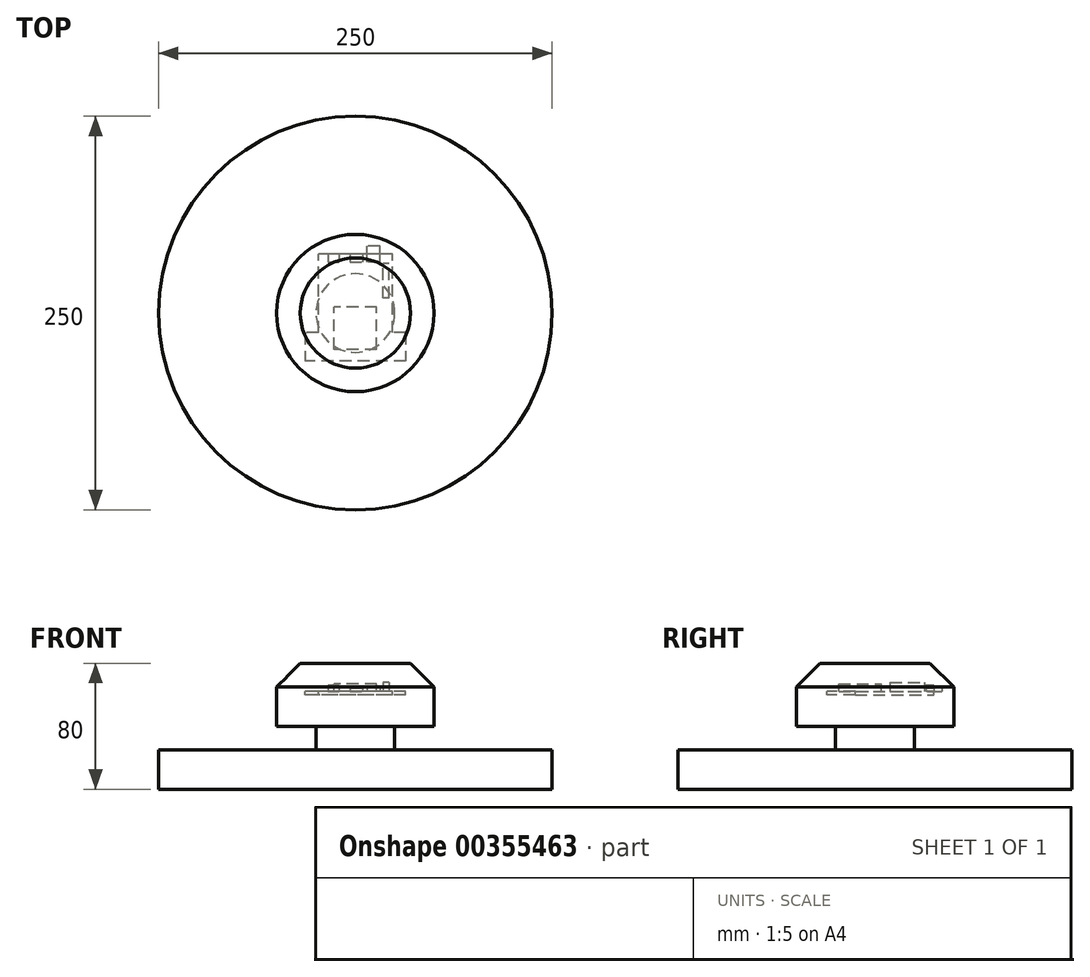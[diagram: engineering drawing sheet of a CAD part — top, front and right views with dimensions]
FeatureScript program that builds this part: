
annotation { "Feature Type Name" : "Feature", "Feature Type Description" : "" }
export const myFeature = defineFeature(function(context is Context, id is Id, definition is map)
    precondition{}
    {
        {
            var Q0;
            Q0=qCreatedBy(makeId("Top.planeOp"),FACE);
            var sketch = newSketch(context, id + "F0", { "sketchPlane" : qUnion([Q0])});
            skLineSegment(sketch, "E0.bottom", {"start": v(13.5, -13.5) * mm, "end": v(-13.5, -13.5) * mm});
            skLineSegment(sketch, "E0.top", {"start": v(13.5, 13.5) * mm, "end": v(-13.5, 13.5) * mm});
            skLineSegment(sketch, "E0.left", {"start": v(13.5, -13.5) * mm, "end": v(13.5, 13.5) * mm});
            skLineSegment(sketch, "E0.right", {"start": v(-13.5, -13.5) * mm, "end": v(-13.5, 13.5) * mm});
            skPoint(sketch, "E0.middle", {"position": v(0, 0) * mm});
            skSolve(sketch);
        }
        {
            var Q0;
            Q0=makeQuery(id+"F0.imprint","IMPRINT",FACE,{"disambiguationData":[TD([[makeQuery(id+"F0.imprint","IMPRINT",EDGE,{"derivedFrom":sQuery(id+"F0.wireOp",EDGE,"E0.bottom")}),-1.0]])]});
            extrude(context, id + "F1", {"entities" : qUnion([Q0]), "oppositeDirection" : true, "depth" : 2 * mm});
        }
        {
            var Q0;
            Q0=makeQuery(id+"F1.opExtrude","CAP_FACE",FACE,{"disambiguationData":[OSD([sQuery(id+"F0.wireOp",EDGE,"E0.bottom"),sQuery(id+"F0.wireOp",EDGE,"E0.top"),sQuery(id+"F0.wireOp",EDGE,"E0.left"),sQuery(id+"F0.wireOp",EDGE,"E0.right")])],"isStart":false});
            cPlane(context, id + "F2", {"entities" : qUnion([Q0]), "cplaneType" : CPlaneType.OFFSET, "offset" : 3 * mm, "width" : 150 * mm, "height" : 150 * mm});
        }
        {
            var Q0;
            Q0=qCreatedBy(id+"F2.planeOp",FACE);
            var sketch = newSketch(context, id + "F3", { "sketchPlane" : qUnion([Q0])});
            skLineSegment(sketch, "E1", {"start": v(0, 0) * mm, "end": v(0, -22) * mm, "construction": true});
            skLineSegment(sketch, "E2.bottom", {"start": v(23.5, 3) * mm, "end": v(-23.5, 3) * mm});
            skLineSegment(sketch, "E2.top", {"start": v(23.5, -47) * mm, "end": v(-23.5, -47) * mm});
            skLineSegment(sketch, "E2.left", {"start": v(23.5, 3) * mm, "end": v(23.5, -47) * mm});
            skLineSegment(sketch, "E2.right", {"start": v(-23.5, 3) * mm, "end": v(-23.5, -47) * mm});
            skPoint(sketch, "E2.middle", {"position": v(0, -22) * mm});
            skSolve(sketch);
        }
        {
            var Q0;
            Q0=makeQuery(id+"F3.imprint","IMPRINT",FACE,{"disambiguationData":[TD([[makeQuery(id+"F3.imprint","IMPRINT",EDGE,{"derivedFrom":sQuery(id+"F3.wireOp",EDGE,"E2.bottom")}),1.0]])]});
            extrude(context, id + "F4", {"entities" : qUnion([Q0]), "depth" : 2 * mm});
        }
        {
            var Q0;
            Q0=makeQuery(id+"F4.opExtrude","CAP_FACE",FACE,{"disambiguationData":[OSD([sQuery(id+"F3.wireOp",EDGE,"E2.bottom"),sQuery(id+"F3.wireOp",EDGE,"E2.top"),sQuery(id+"F3.wireOp",EDGE,"E2.left"),sQuery(id+"F3.wireOp",EDGE,"E2.right")])],"isStart":true});
            var sketch = newSketch(context, id + "F5", { "sketchPlane" : qUnion([Q0])});
            skLineSegment(sketch, "E3", {"start": v(0, -3) * mm, "end": v(0, -12) * mm, "construction": true});
            skPoint(sketch, "E3.endSnap0", {"position": v(0, -3) * mm});
            skLineSegment(sketch, "E4.bottom", {"start": v(32, -3) * mm, "end": v(-32, -3) * mm});
            skLineSegment(sketch, "E4.top", {"start": v(32, -21) * mm, "end": v(-32, -21) * mm});
            skLineSegment(sketch, "E4.left", {"start": v(32, -3) * mm, "end": v(32, -21) * mm});
            skLineSegment(sketch, "E4.right", {"start": v(-32, -3) * mm, "end": v(-32, -21) * mm});
            skPoint(sketch, "E4.middle", {"position": v(0, -12) * mm});
            skSolve(sketch);
        }
        {
            var Q0;
            Q0=makeQuery(id+"F5.imprint","IMPRINT",FACE,{"disambiguationData":[TD([[makeQuery(id+"F5.imprint","IMPRINT",EDGE,{"derivedFrom":sQuery(id+"F5.wireOp",EDGE,"E4.top")}),-1.0]])]});
            extrude(context, id + "F6", {"entities" : qUnion([Q0]), "operationType" : NewBodyOperationType.ADD, "oppositeDirection" : true, "depth" : 2 * mm});
        }
        {
            var Q0;
            Q0=makeQuery(id+"F1.opExtrude","CAP_FACE",FACE,{"disambiguationData":[OSD([sQuery(id+"F0.wireOp",EDGE,"E0.bottom"),sQuery(id+"F0.wireOp",EDGE,"E0.top"),sQuery(id+"F0.wireOp",EDGE,"E0.left"),sQuery(id+"F0.wireOp",EDGE,"E0.right")])],"isStart":false});
            var Q1;
            Q1=makeQuery(id+"F6.boolean.opBoolean","MERGE",FACE,{"derivedFrom":[makeQuery(id+"F4.opExtrude","CAP_FACE",FACE,{"disambiguationData":[OSD([sQuery(id+"F3.wireOp",EDGE,"E2.bottom"),sQuery(id+"F3.wireOp",EDGE,"E2.top"),sQuery(id+"F3.wireOp",EDGE,"E2.left"),sQuery(id+"F3.wireOp",EDGE,"E2.right")])],"isStart":true}),makeQuery(id+"F6.opExtrude","CAP_FACE",FACE,{"disambiguationData":[OSD([sQuery(id+"F5.wireOp",EDGE,"E4.bottom"),sQuery(id+"F5.wireOp",EDGE,"E4.top"),sQuery(id+"F5.wireOp",EDGE,"E4.left"),sQuery(id+"F5.wireOp",EDGE,"E4.right")])],"isStart":true})]});
            extrude(context, id + "F7", {"entities" : qUnion([Q0]), "endBound" : BoundingType.UP_TO_SURFACE, "endBoundEntityFace" : qUnion([Q1]), "depth" : 25 * mm});
        }
        {
            var Q0;
            Q0=makeQuery(id+"F6.boolean.opBoolean","MERGE",FACE,{"derivedFrom":[makeQuery(id+"F4.opExtrude","CAP_FACE",FACE,{"disambiguationData":[OSD([sQuery(id+"F3.wireOp",EDGE,"E2.bottom"),sQuery(id+"F3.wireOp",EDGE,"E2.top"),sQuery(id+"F3.wireOp",EDGE,"E2.left"),sQuery(id+"F3.wireOp",EDGE,"E2.right")])],"isStart":true}),makeQuery(id+"F6.opExtrude","CAP_FACE",FACE,{"disambiguationData":[OSD([sQuery(id+"F5.wireOp",EDGE,"E4.bottom"),sQuery(id+"F5.wireOp",EDGE,"E4.top"),sQuery(id+"F5.wireOp",EDGE,"E4.left"),sQuery(id+"F5.wireOp",EDGE,"E4.right")])],"isStart":true})]});
            var sketch = newSketch(context, id + "F8", { "sketchPlane" : qUnion([Q0])});
            skLineSegment(sketch, "E5", {"start": v(-23.5, 47) * mm, "end": v(-3.5, 47) * mm, "construction": true});
            skLineSegment(sketch, "E6.bottom", {"start": v(-3.5, 47) * mm, "end": v(4.5, 47) * mm});
            skLineSegment(sketch, "E6.top", {"start": v(-3.5, 42) * mm, "end": v(4.5, 42) * mm});
            skLineSegment(sketch, "E6.left", {"start": v(-3.5, 47) * mm, "end": v(-3.5, 42) * mm});
            skLineSegment(sketch, "E6.right", {"start": v(4.5, 47) * mm, "end": v(4.5, 42) * mm});
            skSolve(sketch);
        }
        {
            var Q0;
            Q0=makeQuery(id+"F8.imprint","IMPRINT",FACE,{"disambiguationData":[TD([[makeQuery(id+"F8.imprint","IMPRINT",EDGE,{"derivedFrom":sQuery(id+"F8.wireOp",EDGE,"E6.bottom")}),1.0]])]});
            extrude(context, id + "F9", {"entities" : qUnion([Q0]), "operationType" : NewBodyOperationType.ADD, "depth" : 2 * mm});
        }
        {
            var Q0;
            Q0=makeQuery(id+"F6.boolean.opBoolean","MERGE",FACE,{"derivedFrom":[makeQuery(id+"F4.opExtrude","CAP_FACE",FACE,{"disambiguationData":[OSD([sQuery(id+"F3.wireOp",EDGE,"E2.bottom"),sQuery(id+"F3.wireOp",EDGE,"E2.top"),sQuery(id+"F3.wireOp",EDGE,"E2.left"),sQuery(id+"F3.wireOp",EDGE,"E2.right")])],"isStart":true}),makeQuery(id+"F6.opExtrude","CAP_FACE",FACE,{"disambiguationData":[OSD([sQuery(id+"F5.wireOp",EDGE,"E4.bottom"),sQuery(id+"F5.wireOp",EDGE,"E4.top"),sQuery(id+"F5.wireOp",EDGE,"E4.left"),sQuery(id+"F5.wireOp",EDGE,"E4.right")])],"isStart":true})]});
            var sketch = newSketch(context, id + "F10", { "sketchPlane" : qUnion([Q0])});
            skLineSegment(sketch, "E7", {"start": v(23.5, 47) * mm, "end": v(11.5, 47) * mm, "construction": true});
            skLineSegment(sketch, "E8.bottom", {"start": v(15.5, 42) * mm, "end": v(7.5, 42) * mm});
            skLineSegment(sketch, "E8.top", {"start": v(15.5, 52) * mm, "end": v(7.5, 52) * mm});
            skLineSegment(sketch, "E8.left", {"start": v(15.5, 42) * mm, "end": v(15.5, 52) * mm});
            skLineSegment(sketch, "E8.right", {"start": v(7.5, 42) * mm, "end": v(7.5, 52) * mm});
            skPoint(sketch, "E8.middle", {"position": v(11.5, 47) * mm});
            skSolve(sketch);
        }
        {
            var Q0;
            {var subQ0=sQuery(id+"F10.wireOp",EDGE,"E8.bottom");Q0=makeQuery(id+"F10.imprint","IMPRINT",FACE,{"disambiguationData":[TD([[makeQuery(id+"F10.imprint","IMPRINT",EDGE,{"derivedFrom":subQ0}),-1.0]])]});}
            var Q1;
            {var subQ0=sQuery(id+"F10.wireOp",EDGE,"E8.top");Q1=makeQuery(id+"F10.imprint","IMPRINT",FACE,{"disambiguationData":[TD([[makeQuery(id+"F10.imprint","IMPRINT",EDGE,{"derivedFrom":subQ0}),1.0]])]});}
            extrude(context, id + "F11", {"entities" : qUnion([Q0, Q1]), "operationType" : NewBodyOperationType.ADD, "depth" : 3 * mm});
        }
        {
            var Q0;
            Q0=makeQuery(id+"F6.boolean.opBoolean","MERGE",FACE,{"derivedFrom":[makeQuery(id+"F4.opExtrude","CAP_FACE",FACE,{"disambiguationData":[OSD([sQuery(id+"F3.wireOp",EDGE,"E2.bottom"),sQuery(id+"F3.wireOp",EDGE,"E2.top"),sQuery(id+"F3.wireOp",EDGE,"E2.left"),sQuery(id+"F3.wireOp",EDGE,"E2.right")])],"isStart":true}),makeQuery(id+"F6.opExtrude","CAP_FACE",FACE,{"disambiguationData":[OSD([sQuery(id+"F5.wireOp",EDGE,"E4.bottom"),sQuery(id+"F5.wireOp",EDGE,"E4.top"),sQuery(id+"F5.wireOp",EDGE,"E4.left"),sQuery(id+"F5.wireOp",EDGE,"E4.right")])],"isStart":true})]});
            var sketch = newSketch(context, id + "F12", { "sketchPlane" : qUnion([Q0])});
            skLineSegment(sketch, "E9", {"start": v(23.5, 47) * mm, "end": v(23.5, 30) * mm, "construction": true});
            skLineSegment(sketch, "E10", {"start": v(23.5, 30) * mm, "end": v(19.5, 30) * mm, "construction": true});
            skLineSegment(sketch, "E11.bottom", {"start": v(21.5, 19) * mm, "end": v(17.5, 19) * mm});
            skLineSegment(sketch, "E11.top", {"start": v(21.5, 41) * mm, "end": v(17.5, 41) * mm});
            skLineSegment(sketch, "E11.left", {"start": v(21.5, 19) * mm, "end": v(21.5, 41) * mm});
            skLineSegment(sketch, "E11.right", {"start": v(17.5, 19) * mm, "end": v(17.5, 41) * mm});
            skPoint(sketch, "E11.middle", {"position": v(19.5, 30) * mm});
            skSolve(sketch);
        }
        {
            var Q0;
            Q0=makeQuery(id+"F12.imprint","IMPRINT",FACE,{"disambiguationData":[TD([[makeQuery(id+"F12.imprint","IMPRINT",EDGE,{"derivedFrom":sQuery(id+"F12.wireOp",EDGE,"E11.bottom")}),-1.0]])]});
            extrude(context, id + "F13", {"entities" : qUnion([Q0]), "operationType" : NewBodyOperationType.ADD, "depth" : 6 * mm});
        }
        {
            var Q0;
            Q0=makeQuery(id+"F6.boolean.opBoolean","MERGE",FACE,{"derivedFrom":[makeQuery(id+"F4.opExtrude","CAP_FACE",FACE,{"disambiguationData":[OSD([sQuery(id+"F3.wireOp",EDGE,"E2.bottom"),sQuery(id+"F3.wireOp",EDGE,"E2.top"),sQuery(id+"F3.wireOp",EDGE,"E2.left"),sQuery(id+"F3.wireOp",EDGE,"E2.right")])],"isStart":true}),makeQuery(id+"F6.opExtrude","CAP_FACE",FACE,{"disambiguationData":[OSD([sQuery(id+"F5.wireOp",EDGE,"E4.bottom"),sQuery(id+"F5.wireOp",EDGE,"E4.top"),sQuery(id+"F5.wireOp",EDGE,"E4.left"),sQuery(id+"F5.wireOp",EDGE,"E4.right")])],"isStart":true})]});
            var sketch = newSketch(context, id + "F14", { "sketchPlane" : qUnion([Q0])});
            skLineSegment(sketch, "E12", {"start": v(-23.5, 47) * mm, "end": v(-17.5, 47) * mm, "construction": true});
            skLineSegment(sketch, "E13.bottom", {"start": v(-17.5, 47) * mm, "end": v(-10.5, 47) * mm});
            skLineSegment(sketch, "E13.top", {"start": v(-17.5, 42) * mm, "end": v(-10.5, 42) * mm});
            skLineSegment(sketch, "E13.left", {"start": v(-17.5, 47) * mm, "end": v(-17.5, 42) * mm});
            skLineSegment(sketch, "E13.right", {"start": v(-10.5, 47) * mm, "end": v(-10.5, 42) * mm});
            skSolve(sketch);
        }
        {
            var Q0;
            Q0=makeQuery(id+"F14.imprint","IMPRINT",FACE,{"disambiguationData":[TD([[makeQuery(id+"F14.imprint","IMPRINT",EDGE,{"derivedFrom":sQuery(id+"F14.wireOp",EDGE,"E13.bottom")}),1.0]])]});
            extrude(context, id + "F15", {"entities" : qUnion([Q0]), "operationType" : NewBodyOperationType.ADD, "depth" : 4 * mm});
        }
        {
            var Q0;
            Q0=makeQuery(id+"F6.boolean.opBoolean","MERGE",FACE,{"derivedFrom":[makeQuery(id+"F4.opExtrude","CAP_FACE",FACE,{"disambiguationData":[OSD([sQuery(id+"F3.wireOp",EDGE,"E2.bottom"),sQuery(id+"F3.wireOp",EDGE,"E2.top"),sQuery(id+"F3.wireOp",EDGE,"E2.left"),sQuery(id+"F3.wireOp",EDGE,"E2.right")])],"isStart":false}),makeQuery(id+"F6.opExtrude","CAP_FACE",FACE,{"disambiguationData":[OSD([sQuery(id+"F5.wireOp",EDGE,"E4.bottom"),sQuery(id+"F5.wireOp",EDGE,"E4.top"),sQuery(id+"F5.wireOp",EDGE,"E4.left"),sQuery(id+"F5.wireOp",EDGE,"E4.right")])],"isStart":false})]});
            var sketch = newSketch(context, id + "F16", { "sketchPlane" : qUnion([Q0])});
            skCircle(sketch, "E14", {"center": v(0, -9.53) * mm, "radius": 44.23 * mm, "construction": true});
            skPoint(sketch, "E14.first.point", {"position": v(-23.5, -47) * mm});
            skPoint(sketch, "E14.second.point", {"position": v(23.5, -47) * mm});
            skCircle(sketch, "E15", {"center": v(0, -9.53) * mm, "radius": 47.5 * mm});
            skCircle(sketch, "E16", {"center": v(0, -9.53) * mm, "radius": 50 * mm});
            skSolve(sketch);
        }
        {
            var Q0;
            Q0=makeQuery(id+"F16.imprint","IMPRINT",FACE,{"disambiguationData":[TD([[makeQuery(id+"F16.imprint","IMPRINT",EDGE,{"derivedFrom":sQuery(id+"F16.wireOp",EDGE,"E15")}),-1.0]])]});
            var Q1;
            Q1=makeQuery(id+"F16.imprint","IMPRINT",FACE,{"disambiguationData":[TD([[makeQuery(id+"F16.imprint","IMPRINT",EDGE,{"derivedFrom":sQuery(id+"F16.wireOp",EDGE,"E15")}),1.0]])]});
            var Q2;
            {var subQ3=sQuery(id+"F3.wireOp",EDGE,"E2.top");Q2=makeQuery(id+"F16.imprint","IMPRINT",FACE,{"disambiguationData":[TD([[makeQuery(id+"F16.imprint","IMPRINT",EDGE,{"derivedFrom":makeQuery(id+"F4.opExtrude","CAP_EDGE",EDGE,{"disambiguationData":[OSD([subQ3])],"isStart":false})}),-1.0]])]});}
            extrude(context, id + "F17", {"entities" : qUnion([Q0, Q1, Q2]), "depth" : 20 * mm, "hasSecondDirection" : true, "secondDirectionOppositeDirection" : true, "secondDirectionDepth" : 20 * mm});
        }
        {
            var Q0;
            Q0=makeQuery(id+"F17.opExtrude","CAP_EDGE",EDGE,{"disambiguationData":[OSD([sQuery(id+"F16.wireOp",EDGE,"E16")])],"isStart":true});
            chamfer(context, id + "F18", {"entities" : qUnion([Q0]), "width" : 15 * mm, "tangentPropagation" : true});
        }
        {
            var Q0;
            Q0=makeQuery(id+"F17.opExtrude","CAP_FACE",FACE,{"disambiguationData":[OSD([sQuery(id+"F16.wireOp",EDGE,"E16")])],"isStart":false});
            var sketch = newSketch(context, id + "F19", { "sketchPlane" : qUnion([Q0])});
            skCircle(sketch, "E17", {"center": v(0, -9.53) * mm, "radius": 25 * mm});
            skSolve(sketch);
        }
        {
            var Q0;
            Q0 = qSketchRegion(id + "F19", true);
            extrude(context, id + "F20", {"entities" : qUnion([Q0]), "depth" : 15 * mm});
        }
        {
            var Q0;
            Q0=makeQuery(id+"F20.opExtrude","CAP_FACE",FACE,{"disambiguationData":[OSD([sQuery(id+"F19.wireOp",EDGE,"E17")])],"isStart":false});
            var sketch = newSketch(context, id + "F21", { "sketchPlane" : qUnion([Q0])});
            skCircle(sketch, "E18", {"center": v(0, -9.53) * mm, "radius": 125 * mm});
            skSolve(sketch);
        }
        {
            var Q0;
            Q0=makeQuery(id+"F21.imprint","IMPRINT",FACE,{"disambiguationData":[TD([[makeQuery(id+"F21.imprint","IMPRINT",EDGE,{"derivedFrom":sQuery(id+"F21.wireOp",EDGE,"E18")}),1.0]])]});
            var Q1;
            Q1=makeQuery(id+"F21.imprint","IMPRINT",FACE,{"disambiguationData":[TD([[makeQuery(id+"F21.imprint","IMPRINT",EDGE,{"derivedFrom":makeQuery(id+"F20.opExtrude","CAP_EDGE",EDGE,{"disambiguationData":[OSD([sQuery(id+"F19.wireOp",EDGE,"E17")])],"isStart":false})}),1.0]])]});
            extrude(context, id + "F22", {"entities" : qUnion([Q0, Q1]), "operationType" : NewBodyOperationType.ADD, "depth" : 25 * mm});
        }
    });
